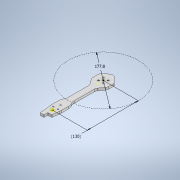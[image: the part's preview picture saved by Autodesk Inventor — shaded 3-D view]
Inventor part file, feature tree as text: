
AUTODESK INVENTOR PART (.ipt)
format: ipt  version: 2020 (Build 240168000, 168)  size: 248,832 bytes
history: native  units: in
note: dims shown in document units (in); Inventor stores cm internally (conversion verified against a paired STEP export)
features: sketch x3, extrude x2, fillet x2
ambient origin geometry x8: Origin, YZ Plane, XZ Plane, XY Plane, X Axis, Y Axis, Z Axis, Center Point
bodies: Body1 (feature_tree)
feature tree (7):
  extrude  "Extrusion1"  Depth=0.2362in
  sketch  "Sketch4"  dims[d7=0.4724in d8=5.1181in d9=7.0in d10=5.1181in]
  extrude  "Extrusion2"  Depth=5.1181in
  fillet  "Fillet2"  Radius=7.0in
  fillet  "Fillet3"  Radius=5.1181in
  sketch  "Sketch3"  dims[d2=0.2362in d3=0.0in d4=0.8352in]
  sketch  "Sketch5"  dims[d11=0.2953in d12=0.2953in d13=0.9835in d14=0.9835in d15=0.989in d16=0.1181in d17=0.0in d18=0.3937in d20=0.3937in d21=0.7874in]
